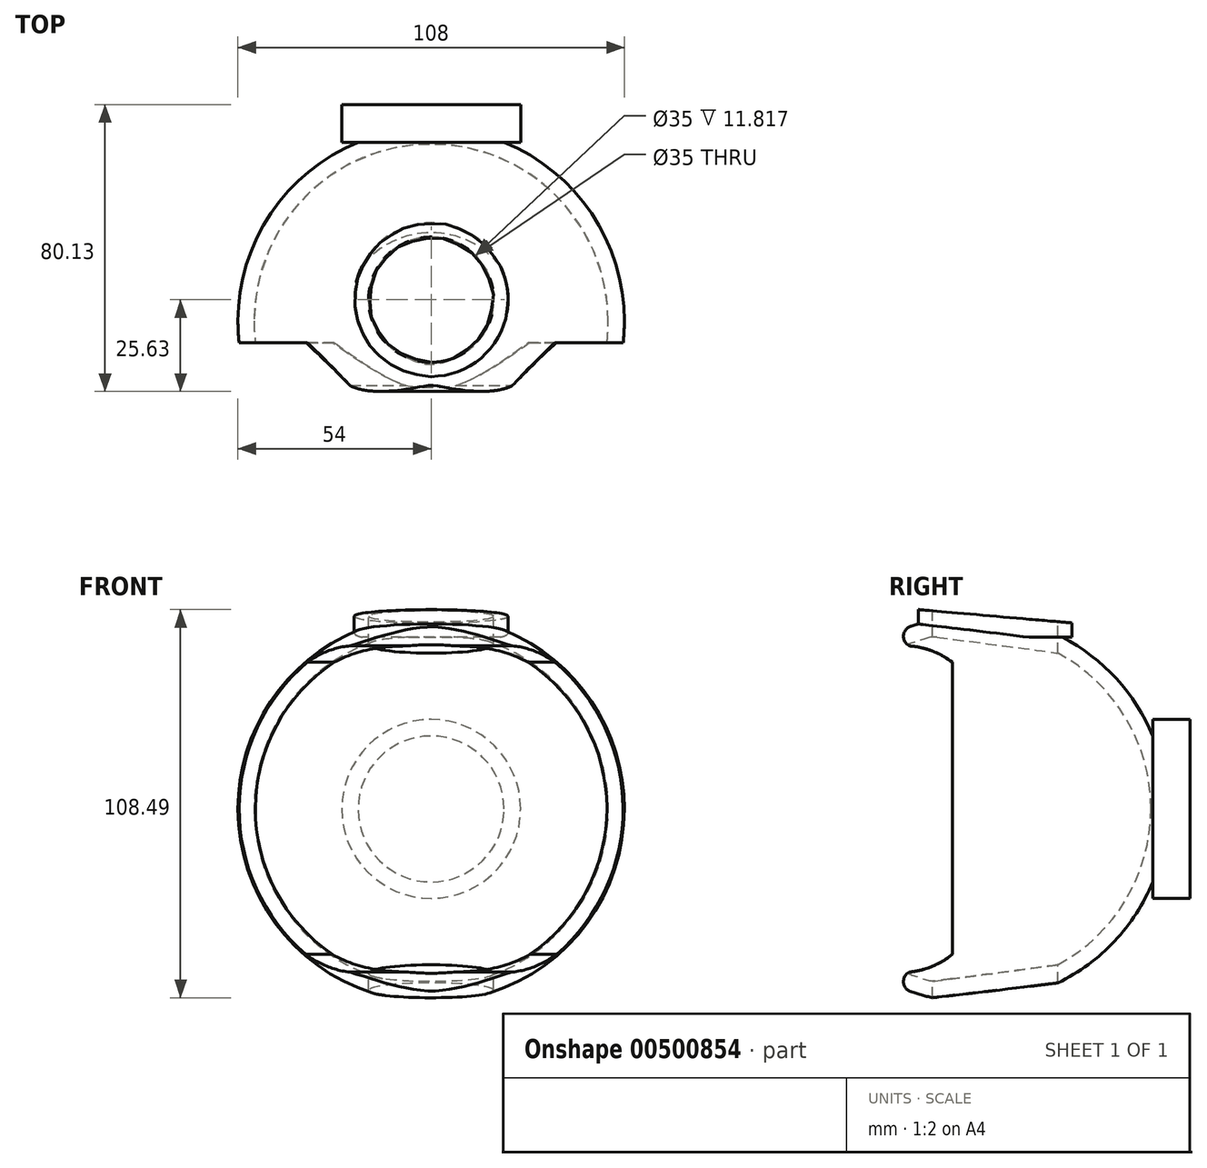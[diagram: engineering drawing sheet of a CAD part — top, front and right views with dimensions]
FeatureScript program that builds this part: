
annotation { "Feature Type Name" : "Feature", "Feature Type Description" : "" }
export const myFeature = defineFeature(function(context is Context, id is Id, definition is map)
    precondition{}
    {
        {
            var Q0;
            Q0=qCreatedBy(makeId("Front.planeOp"),FACE);
            var sketch = newSketch(context, id + "F0", { "sketchPlane" : qUnion([Q0])});
            skArc(sketch, "E0", {"start": v(54, 0) * mm, "mid": v(0, 54) * mm, "end": v(-54, 0) * mm});
            skArc(sketch, "E1", {"start": v(49.5, 0) * mm, "mid": v(0, 49.5) * mm, "end": v(-49.5, 0) * mm});
            skLineSegment(sketch, "E2", {"start": v(-54, 0) * mm, "end": v(-49.5, 0) * mm});
            skLineSegment(sketch, "E3", {"start": v(54, 0) * mm, "end": v(49.5, 0) * mm});
            skSolve(sketch);
        }
        {
            var Q0;
            Q0=qSketchRegion(id+"F0",true);
            var Q1;
            Q1=sQuery(id+"F0.wireOp",EDGE,"E2");
            revolve(context, id + "F1", {"entities" : qUnion([Q0]), "axis" : qUnion([Q1]), "revolveType" : RevolveType.FULL});
        }
        {
            var Q0;
            Q0=qCreatedBy(makeId("Right.planeOp"),FACE);
            cPlane(context, id + "F2", {"entities" : qUnion([Q0]), "cplaneType" : CPlaneType.OFFSET, "offset" : 54 * mm, "width" : 150 * mm, "height" : 150 * mm});
        }
        {
            var Q0;
            Q0=qCreatedBy(id+"F2.planeOp",FACE);
            var sketch = newSketch(context, id + "F3", { "sketchPlane" : qUnion([Q0])});
            skCircle(sketch, "E4", {"center": v(0, 0) * mm, "radius": 54 * mm});
            skCircle(sketch, "E5", {"center": v(0, 0) * mm, "radius": 49 * mm});
            skPoint(sketch, "E6", {"position": v(54, 0) * mm});
            skLineSegment(sketch, "E7", {"start": v(54, 0) * mm, "end": v(54, 65) * mm, "construction": true});
            skLineSegment(sketch, "E8", {"start": v(54, 0) * mm, "end": v(54, -65) * mm, "construction": true});
            skPoint(sketch, "E9", {"position": v(0, 54) * mm});
            skPoint(sketch, "E10", {"position": v(-18, 54) * mm});
            skPoint(sketch, "E11", {"position": v(0, 49) * mm});
            skPoint(sketch, "E12", {"position": v(-6, 49) * mm});
            skLineSegment(sketch, "E13", {"start": v(-18, 54) * mm, "end": v(-18, -50.91) * mm, "construction": true});
            skLineSegment(sketch, "E14", {"start": v(-18, 50.91) * mm, "end": v(-18, 45.57) * mm});
            skLineSegment(sketch, "E15", {"start": v(-18, -50.91) * mm, "end": v(-18, -45.57) * mm});
            skPoint(sketch, "E16", {"position": v(-6, 41) * mm});
            skPoint(sketch, "E17", {"position": v(-6, -48.63) * mm});
            skPoint(sketch, "E18", {"position": v(-6, -40.63) * mm});
            skLineSegment(sketch, "E19", {"start": v(-6, 41) * mm, "end": v(-6, -40.63) * mm});
            skArc(sketch, "E20", {"start": v(-18, -45.57) * mm, "mid": v(-11.63, -44) * mm, "end": v(-6, -40.63) * mm});
            skArc(sketch, "E21", {"start": v(-6, 41) * mm, "mid": v(-11.66, 44.18) * mm, "end": v(-18, 45.57) * mm});
            skArc(sketch, "E22", {"start": v(-18, 50.91) * mm, "mid": v(-19.63, 48.24) * mm, "end": v(-18, 45.57) * mm});
            skArc(sketch, "E23", {"start": v(-18, -45.57) * mm, "mid": v(-19.63, -48.24) * mm, "end": v(-18, -50.91) * mm});
            skSolve(sketch);
        }
        {
            var Q0;
            Q0=makeQuery(id+"F3.imprint","IMPRINT",FACE,{"disambiguationData":[TD([[makeQuery(id+"F3.imprint","IMPRINT",EDGE,{"derivedFrom":sQuery(id+"F3.wireOp",EDGE,"E19")}),-1.0]])]});
            var Q1;
            {var subQ0=sQuery(id+"F3.wireOp",EDGE,"E22");Q1=makeQuery(id+"F3.imprint","IMPRINT",FACE,{"disambiguationData":[TD([[makeQuery(id+"F3.imprint","IMPRINT",EDGE,{"derivedFrom":subQ0}),-1.0]])]});}
            extrude(context, id + "F4", {"entities" : qUnion([Q0, Q1]), "operationType" : NewBodyOperationType.REMOVE, "oppositeDirection" : true, "depth" : 108 * mm});
        }
        {
            var Q0;
            Q0=qCreatedBy(makeId("Top.planeOp"),FACE);
            cPlane(context, id + "F5", {"entities" : qUnion([Q0]), "cplaneType" : CPlaneType.OFFSET, "offset" : 54 * mm, "width" : 150 * mm, "height" : 150 * mm});
        }
        {
            var Q0;
            Q0=qCreatedBy(id+"F5.planeOp",FACE);
            var sketch = newSketch(context, id + "F6", { "sketchPlane" : qUnion([Q0])});
            skPoint(sketch, "E24", {"position": v(0, -18) * mm});
            skPoint(sketch, "E25", {"position": v(0, 6) * mm});
            skCircle(sketch, "E26", {"center": v(0, 6) * mm, "radius": 17.5 * mm});
            skSolve(sketch);
        }
        {
            var Q0;
            Q0=qSketchRegion(id+"F6",true);
            extrude(context, id + "F7", {"entities" : qUnion([Q0]), "operationType" : NewBodyOperationType.REMOVE, "oppositeDirection" : true, "depth" : 108 * mm});
        }
        {
            var Q0;
            Q0=qCreatedBy(makeId("Front.planeOp"),FACE);
            cPlane(context, id + "F8", {"entities" : qUnion([Q0]), "cplaneType" : CPlaneType.OFFSET, "offset" : 50 * mm, "oppositeDirection" : true, "width" : 150 * mm, "height" : 150 * mm});
        }
        {
            var Q0;
            Q0=qCreatedBy(id+"F8.planeOp",FACE);
            var sketch = newSketch(context, id + "F9", { "sketchPlane" : qUnion([Q0])});
            skCircle(sketch, "E27", {"center": v(0, 0) * mm, "radius": 25 * mm});
            skSolve(sketch);
        }
        {
            var Q0;
            Q0=qSketchRegion(id+"F9",true);
            extrude(context, id + "F10", {"entities" : qUnion([Q0]), "operationType" : NewBodyOperationType.ADD, "oppositeDirection" : true, "depth" : 10.5 * mm});
        }
        {
            var Q0;
            Q0=qCreatedBy(id+"F5.planeOp",FACE);
            cPlane(context, id + "F11", {"entities" : qUnion([Q0]), "cplaneType" : CPlaneType.OFFSET, "offset" : 4 * mm, "width" : 150 * mm, "height" : 150 * mm});
        }
        {
            var Q0;
            Q0=qCreatedBy(id+"F11.planeOp",FACE);
            var sketch = newSketch(context, id + "F12", { "sketchPlane" : qUnion([Q0])});
            skCircle(sketch, "E28.0", {"center": v(0, 6) * mm, "radius": 17.5 * mm});
            skCircle(sketch, "E29", {"center": v(0, 6) * mm, "radius": 21.5 * mm});
            skSolve(sketch);
        }
        {
            var Q0;
            Q0=qSketchRegion(id+"F12",true);
            extrude(context, id + "F13", {"entities" : qUnion([Q0]), "operationType" : NewBodyOperationType.ADD, "oppositeDirection" : true, "depth" : 10 * mm});
        }
        {
            var Q0;
            Q0=qCreatedBy(makeId("Right.planeOp"),FACE);
            var sketch = newSketch(context, id + "F14", { "sketchPlane" : qUnion([Q0])});
            skFitSpline(sketch, "E30.0", {"points": [v(15.48, 48) * mm, v(14.66, 48.1) * mm, v(12.99, 48.31) * mm, v(10.81, 48.58) * mm, v(9.03, 48.8) * mm, v(7.21, 49.02) * mm, v(4.96, 49.3) * mm, v(2.72, 49.57) * mm, v(0.93, 49.78) * mm, v(-0.82, 50) * mm, v(-2.5, 50.2) * mm, v(-4.12, 50.4) * mm, v(-5.3, 50.53) * mm, v(-6.45, 50.67) * mm, v(-7.89, 50.84) * mm, v(-9.22, 51) * mm, v(-10.44, 51.14) * mm, v(-11.58, 51.27) * mm, v(-12.8, 51.41) * mm, v(-13.79, 51.53) * mm, v(-14.42, 51.6) * mm, v(-14.94, 51.66) * mm, v(-15.38, 51.71) * mm, v(-15.5, 51.73) * mm, v(-15.5, 51.73) * mm]});
            skPoint(sketch, "E31", {"position": v(-15.5, 55.73) * mm});
            skLineSegment(sketch, "E32.0", {"start": v(15.48, 48) * mm, "end": v(27.5, 48) * mm});
            skPoint(sketch, "E33", {"position": v(27.5, 52) * mm});
            skLineSegment(sketch, "E34", {"start": v(-15.5, 55.73) * mm, "end": v(27.5, 52) * mm});
            skLineSegment(sketch, "E35.0", {"start": v(-15.5, 58) * mm, "end": v(27.5, 58) * mm});
            skLineSegment(sketch, "E36", {"start": v(27.5, 58) * mm, "end": v(27.5, 52) * mm});
            skLineSegment(sketch, "E37", {"start": v(-15.5, 58) * mm, "end": v(-15.5, 55.73) * mm});
            skLineSegment(sketch, "E38", {"start": v(-15.5, 58) * mm, "end": v(-16.5, 58) * mm});
            skLineSegment(sketch, "E39", {"start": v(-16.5, 58) * mm, "end": v(-16.5, 55.72) * mm});
            skLineSegment(sketch, "E40", {"start": v(-16.5, 55.72) * mm, "end": v(-15.5, 55.73) * mm});
            skSolve(sketch);
        }
        {
            var Q0;
            Q0=qSketchRegion(id+"F14",true);
            extrude(context, id + "F15", {"entities" : qUnion([Q0]), "operationType" : NewBodyOperationType.REMOVE, "endBound" : BoundingType.SYMMETRIC, "oppositeDirection" : true, "depth" : 45 * mm});
        }
    });
